# Revit family: 1
name_source: partatom
category: Furniture
revit_build: Autodesk Revit 2017 (Build: 20160225_1515(x64)
units: mm (PartAtom-declared; Revit-internal decimal feet)

## family parameters
Always vertical = Yes
Cut with Voids When Loaded = No
OmniClass Number = 23.40.20.00
OmniClass Title = General Furniture and Specialties
Room Calculation Point = No
Shared = No
Work Plane-Based = No

## types (80) — shared parameters
Assembly Code = E2020200
D = 2400 mm  [stored 7.87402 ft]
H = 1700 mm  [stored 5.57743 ft]
Keynote = 12490
Kind = Individual booth unit
Leg = okm_Z637
Manufacturer = Okamura Corporation
Product Categories = Muffle
Product Number = MM53BW
Sofa_Leg = okm_PL7
Trim = okm_ZC11
URL = http://www.okamura.co.jp
W = 1400 mm  [stored 4.59318 ft]

## per-type parameters (varying)
| type | Desktop | Panel_Exterior | Panel_Interior | Sofa_Back/Seat | Sofa_Cushion |
| MAJ8(White/Peach_Mono) | okm_MG99 | okm_F005 | okm_F005 | okm_F005 | okm_F005 |
| MAJ1(White/Oats_Mono) | okm_MG99 | okm_F026 | okm_F026 | okm_F026 | okm_F026 |
| MAJ2(White/Mushroom_Mono) | okm_MG99 | okm_F025 | okm_F025 | okm_F025 | okm_F025 |
| MAJ0(White/Blackberry_Mono) | okm_MG99 | okm_F013 | okm_F013 | okm_F013 | okm_F013 |
| MAJ3(White/Huckleberry_Mono) | okm_MG99 | okm_F007 | okm_F007 | okm_F007 | okm_F007 |
| MAJ9(White/Indigo_Mono) | okm_MG99 | okm_F029 | okm_F029 | okm_F029 | okm_F029 |
| MAJ4(White/Sage_Mono) | okm_MG99 | okm_F002 | okm_F002 | okm_F002 | okm_F002 |
| MAJ5(White/Grape_Mono) | okm_MG99 | okm_F015 | okm_F015 | okm_F015 | okm_F015 |
| MAJ6(White/Chamomile_Mono) | okm_MG99 | okm_F027 | okm_F027 | okm_F027 | okm_F027 |
| MAJ7(White/Pumpkin_Mono) | okm_MG99 | okm_F010 | okm_F010 | okm_F010 | okm_F010 |
| MZ14(White/Sage/Vanilla) | okm_MG99 | okm_F002 | okm_F024 | okm_F024 | okm_F002 |
| MZ13(White/Huckleberry/Vanilla) | okm_MG99 | okm_F007 | okm_F024 | okm_F024 | okm_F007 |
| MZ17(White/Pumpkin/Vanilla) | okm_MG99 | okm_F010 | okm_F024 | okm_F024 | okm_F010 |
| MZ20(White/Blackberry/Vanilla) | okm_MG99 | okm_F013 | okm_F024 | okm_F024 | okm_F013 |
| MZ15(White/Grape/Vanilla) | okm_MG99 | okm_F015 | okm_F024 | okm_F015 | okm_F015 |
| MZ12(White/Mushroom/Vanilla) | okm_MG99 | okm_F025 | okm_F024 | okm_F024 | okm_F025 |
| MZ16(White/Chamomile/Vanilla) | okm_MG99 | okm_F027 | okm_F024 | okm_F024 | okm_F027 |
| MZ19(White/Indigo/Vanilla) | okm_MG99 | okm_F029 | okm_F024 | okm_F024 | okm_F029 |
| MZ11(White/Oats/Vanilla) | okm_MG99 | okm_F026 | okm_F024 | okm_F024 | okm_F026 |
| MZ18(White/Peach/Vanilla) | okm_MG99 | okm_F005 | okm_F024 | okm_F024 | okm_F005 |
| MAK0(Neo Wood Light/Blackberry_Mono) | okm_MK37 | okm_F013 | okm_F013 | okm_F013 | okm_F013 |
| MAK1(Neo Wood Light/Oats_Mono) | okm_MK37 | okm_F026 | okm_F026 | okm_F026 | okm_F026 |
| MAL2(Neo Wood Medium/Mushroom_Mono) | okm_MK38 | okm_F025 | okm_F025 | okm_F025 | okm_F025 |
| MAL3(Neo Wood Medium/Huckleberry_Mono) | okm_MK38 | okm_F007 | okm_F007 | okm_F007 | okm_F007 |
| MAK4(Neo Wood Light/Sage_Mono) | okm_MK37 | okm_F002 | okm_F002 | okm_F002 | okm_F002 |
| MAK5(Neo Wood Light/Grape_Mono) | okm_MK37 | okm_F015 | okm_F015 | okm_F015 | okm_F015 |
| MAK6(Neo Wood Light/Chamomile_Mono) | okm_MK37 | okm_F027 | okm_F027 | okm_F027 | okm_F027 |
| MAK7(Neo Wood Light/Pumpkin_Mono) | okm_MK37 | okm_F010 | okm_F010 | okm_F010 | okm_F010 |
| MAK8(Neo Wood Light/Peach_Mono) | okm_MK37 | okm_F005 | okm_F005 | okm_F005 | okm_F005 |
| MAK9(Neo Wood Light/Indigo_Mono) | okm_MK37 | okm_F029 | okm_F029 | okm_F029 | okm_F029 |
| MAL1(Neo Wood Medium/Oats_Mono) | okm_MK38 | okm_F026 | okm_F026 | okm_F026 | okm_F026 |
| MAK3(Neo Wood Light/Huckleberry_Mono) | okm_MK37 | okm_F007 | okm_F007 | okm_F007 | okm_F007 |
| MAK2(Neo Wood Light/Mushroom_Mono) | okm_MK37 | okm_F025 | okm_F025 | okm_F025 | okm_F025 |
| MAL4(Neo Wood Medium/Sage_Mono) | okm_MK38 | okm_F002 | okm_F002 | okm_F002 | okm_F002 |
| MAM1(Neo Wood Dark/Oats_Mono) | okm_MK39 | okm_F026 | okm_F026 | okm_F026 | okm_F026 |
| MAL5(Neo Wood Medium/Grape_Mono) | okm_MK38 | okm_F015 | okm_F015 | okm_F015 | okm_F015 |
| MAL6(Neo Wood Medium/Chamomile_Mono) | okm_MK38 | okm_F027 | okm_F027 | okm_F027 | okm_F027 |
| MAL7(Neo Wood Medium/Pumpkin_Mono) | okm_MK38 | okm_F010 | okm_F010 | okm_F010 | okm_F010 |
| MAL8(Neo Wood Medium/Peach_Mono) | okm_MG99 | okm_F027 | okm_F024 | okm_F024 | okm_F027 |
| MAL9(Neo Wood Medium/Indigo_Mono) | okm_MK38 | okm_F029 | okm_F029 | okm_F029 | okm_F029 |
| MAL0(Neo Wood Medium/Blackberry_Mono) | okm_MK38 | okm_F013 | okm_F013 | okm_F013 | okm_F013 |
| MAM0(Neo Wood Dark/Blackberry_Mono) | okm_MK39 | okm_F013 | okm_F013 | okm_F013 | okm_F013 |
| MAM2(Neo Wood Dark/Mushroom_Mono) | okm_MK39 | okm_F025 | okm_F025 | okm_F025 | okm_F025 |
| MAM3(Neo Wood Dark/Huckleberry_Mono) | okm_MK39 | okm_F007 | okm_F007 | okm_F007 | okm_F007 |
| MAM4(Neo Wood Dark/Sage_Mono) | okm_MK39 | okm_F002 | okm_F002 | okm_F002 | okm_F002 |
| MAM5(Neo Wood Dark/Grape_Mono) | okm_MK39 | okm_F015 | okm_F015 | okm_F015 | okm_F015 |
| MAM6(Neo Wood Dark/Chamomile_Mono) | okm_MK39 | okm_F027 | okm_F027 | okm_F027 | okm_F027 |
| MAM7(Neo Wood Dark/Pumpkin_Mono) | okm_MK39 | okm_F010 | okm_F010 | okm_F010 | okm_F010 |
| MAM8(Neo Wood Dark/Peach_Mono) | okm_MK39 | okm_F005 | okm_F005 | okm_F005 | okm_F005 |
| MAM9(Neo Wood Dark/Indigo_Mono) | okm_MK39 | okm_F029 | okm_F029 | okm_F029 | okm_F029 |
| MZ21(Neo Wood Light/Oats/Vanilla) | okm_MK37 | okm_F026 | okm_F024 | okm_F024 | okm_F026 |
| MZ22(Neo Wood Light/Mushroom/Vanilla) | okm_MK37 | okm_F025 | okm_F024 | okm_F024 | okm_F025 |
| MZ23(Neo Wood Light/Huckleberry/Vanilla) | okm_MK37 | okm_F007 | okm_F024 | okm_F024 | okm_F007 |
| MZ24(Neo Wood Light/Sage/Vanilla) | okm_MK37 | okm_F002 | okm_F024 | okm_F024 | okm_F002 |
| MZ25(Neo Wood Light/Grape/Vanilla) | okm_MK37 | okm_F015 | okm_F024 | okm_F024 | okm_F015 |
| MZ26(Neo Wood Light/Chamomile/Vanilla) | okm_MK37 | okm_F027 | okm_F024 | okm_F024 | okm_F027 |
| MZ27(Neo Wood Light/Pumpkin/Vanilla) | okm_MK37 | okm_F010 | okm_F024 | okm_F024 | okm_F010 |
| MZ28(Neo Wood Light/Peach/Vanilla) | okm_MK37 | okm_F005 | okm_F024 | okm_F024 | okm_F005 |
| MZ29(Neo Wood Light/Indigo/Vanilla) | okm_MK37 | okm_F029 | okm_F024 | okm_F024 | okm_F029 |
| MZ30(Neo Wood Light/Blackberry/Vanilla) | okm_MK37 | okm_F013 | okm_F024 | okm_F024 | okm_F013 |
| MZ31(Neo Wood Medium/Oats/Vanilla) | okm_MK38 | okm_F026 | okm_F024 | okm_F024 | okm_F026 |
| MZ32(Neo Wood Medium/Mushroom/Vanilla) | okm_MK38 | okm_F025 | okm_F024 | okm_F024 | okm_F025 |
| MZ33(Neo Wood Medium/Huckleberry/Vanilla) | okm_MK38 | okm_F007 | okm_F024 | okm_F024 | okm_F007 |
| MZ34(Neo Wood Medium/Sage/Vanilla) | okm_MK38 | okm_F002 | okm_F024 | okm_F024 | okm_F002 |
| MZ35(Neo Wood Medium/Grape/Vanilla) | okm_MK38 | okm_F015 | okm_F024 | okm_F024 | okm_F015 |
| MZ36(Neo Wood Medium/Chamomile/Vanilla) | okm_MK38 | okm_F027 | okm_F024 | okm_F024 | okm_F027 |
| MZ37(Neo Wood Medium/Pumpkin/Vanilla) | okm_MK38 | okm_F010 | okm_F024 | okm_F024 | okm_F010 |
| MZ38(Neo Wood Medium/Peach/Vanilla) | okm_MK38 | okm_F005 | okm_F024 | okm_F024 | okm_F005 |
| MZ39(Neo Wood Medium/Indigo/Vanilla) | okm_MK38 | okm_F029 | okm_F024 | okm_F024 | okm_F029 |
| MZ40(Neo Wood Medium/Blackberry/Vanilla) | okm_MK38 | okm_F013 | okm_F024 | okm_F024 | okm_F013 |
| MZ50(Neo Wood Dark/Blackberry/Vanilla) | okm_MK39 | okm_F013 | okm_F024 | okm_F024 | okm_F013 |
| MZ41(Neo Wood Dark/Oats/Vanilla) | okm_MK39 | okm_F026 | okm_F024 | okm_F024 | okm_F026 |
| MZ42(Neo Wood Dark/Mushroom/Vanilla) | okm_MK39 | okm_F025 | okm_F024 | okm_F024 | okm_F025 |
| MZ43(Neo Wood Dark/Huckleberry/Vanilla) | okm_MK39 | okm_F007 | okm_F024 | okm_F024 | okm_F007 |
| MZ44(Neo Wood Dark/Sage/Vanilla) | okm_MK39 | okm_F002 | okm_F024 | okm_F024 | okm_F002 |
| MZ45(Neo Wood Dark/Grape/Vanilla) | okm_MK39 | okm_F015 | okm_F024 | okm_F024 | okm_F015 |
| MZ46(Neo Wood Dark/Chamomile/Vanilla) | okm_MK39 | okm_F027 | okm_F024 | okm_F024 | okm_F027 |
| MZ47(Neo Wood Dark/Pumpkin/Vanilla) | okm_MK39 | okm_F010 | okm_F024 | okm_F024 | okm_F010 |
| MZ48(Neo Wood Dark/Peach/Vanilla) | okm_MK39 | okm_F005 | okm_F024 | okm_F024 | okm_F005 |
| MZ49(Neo Wood Dark/Indigo/Vanilla) | okm_MK39 | okm_F029 | okm_F024 | okm_F024 | okm_F029 |

note: [stored X ft] marks values corroborated as IEEE doubles in the binary element streams (Revit-internal decimal feet)

## geometry (parser evidence)
native form markers: Sweep x3
no freeform markers — native parametric forms only
